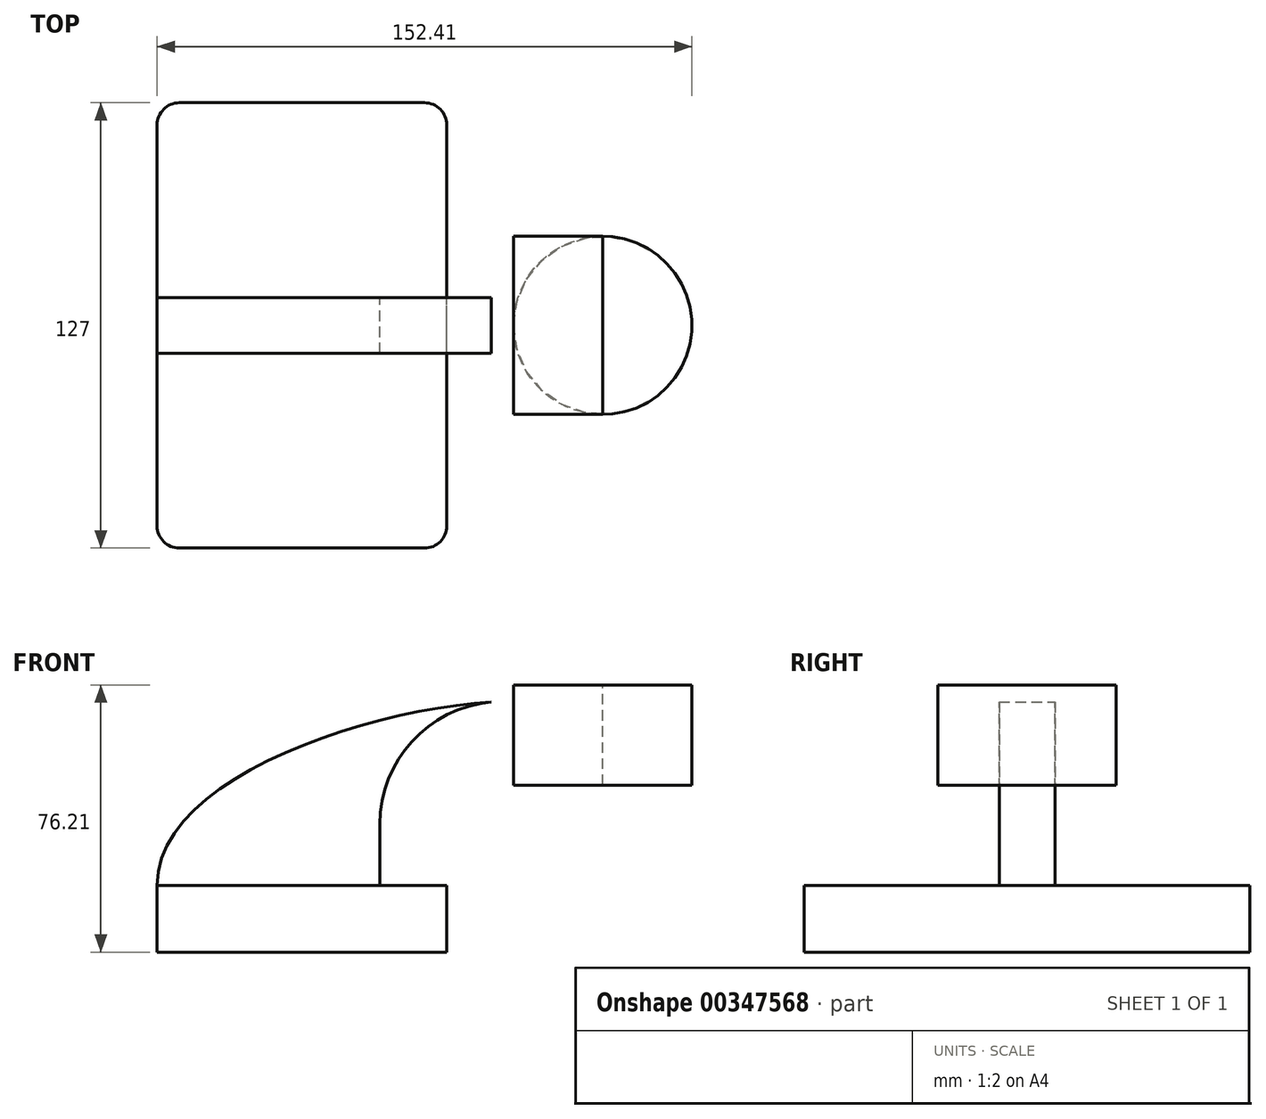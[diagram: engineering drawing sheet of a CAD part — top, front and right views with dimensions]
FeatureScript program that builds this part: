
annotation { "Feature Type Name" : "Feature", "Feature Type Description" : "" }
export const myFeature = defineFeature(function(context is Context, id is Id, definition is map)
    precondition{}
    {
        {
            var Q0;
            Q0=qCreatedBy(makeId("Front.planeOp"),FACE);
            var sketch = newSketch(context, id + "F0", { "sketchPlane" : qUnion([Q0])});
            skLineSegment(sketch, "E0.bottom", {"start": v(-41.28, 9.52) * mm, "end": v(41.27, 9.53) * mm});
            skLineSegment(sketch, "E0.top", {"start": v(-41.28, -9.53) * mm, "end": v(41.28, -9.53) * mm});
            skLineSegment(sketch, "E0.left", {"start": v(-41.28, 9.52) * mm, "end": v(-41.27, -9.53) * mm});
            skLineSegment(sketch, "E0.right", {"start": v(41.28, 9.53) * mm, "end": v(41.28, -9.52) * mm});
            skPoint(sketch, "E0.middle", {"position": v(0, 0) * mm});
            skLineSegment(sketch, "E1.bottom", {"start": v(60.32, 66.68) * mm, "end": v(111.12, 66.68) * mm});
            skLineSegment(sketch, "E1.top", {"start": v(60.32, 38.1) * mm, "end": v(111.12, 38.1) * mm});
            skLineSegment(sketch, "E1.left", {"start": v(60.32, 66.68) * mm, "end": v(60.32, 38.1) * mm});
            skLineSegment(sketch, "E1.right", {"start": v(111.12, 66.68) * mm, "end": v(111.12, 38.1) * mm});
            skPoint(sketch, "E1.middle", {"position": v(85.72, 52.39) * mm});
            skArc(sketch, "E2", {"start": v(41.27, 27) * mm, "mid": v(45.92, 38.23) * mm, "end": v(57.15, 42.88) * mm});
            skLineSegment(sketch, "E3", {"start": v(57.15, 42.88) * mm, "end": v(85.71, 42.88) * mm});
            skLineSegment(sketch, "E4", {"start": v(41.27, 27) * mm, "end": v(41.27, 9.53) * mm});
            skLineSegment(sketch, "E5.0", {"start": v(22.23, 27) * mm, "end": v(22.23, 9.53) * mm});
            skLineSegment(sketch, "E6.0", {"start": v(57.15, 61.93) * mm, "end": v(85.71, 61.93) * mm});
            skArc(sketch, "E6.1", {"start": v(22.22, 27) * mm, "mid": v(32.45, 51.7) * mm, "end": v(57.15, 61.93) * mm});
            skLineSegment(sketch, "E7", {"start": v(85.72, 38.1) * mm, "end": v(85.71, 66.68) * mm});
            skFitSpline(sketch, "E8", {"points": [v(-41.28, 9.52) * mm, v(57.15, 61.93) * mm], "startDerivative": vector(-0.23, 93.6) * mm, "endDerivative": vector(107.82, 3.43) * mm});
            skSolve(sketch);
        }
        {
            var Q0;
            Q0=makeQuery(id+"F0.imprint","IMPRINT",FACE,{"disambiguationData":[TD([[makeQuery(id+"F0.imprint","IMPRINT",EDGE,{"derivedFrom":sQuery(id+"F0.wireOp",EDGE,"E0.top")}),1.0]])]});
            extrude(context, id + "F1", {"entities" : qUnion([Q0]), "endBound" : BoundingType.SYMMETRIC, "depth" : 127 * mm});
        }
        {
            var Q0;
            {var subQ4=sQuery(id+"F0.wireOp",EDGE,"E7");Q0=makeQuery(id+"F0.imprint","IMPRINT",FACE,{"disambiguationData":[TD([[makeQuery(id+"F0.imprint","IMPRINT",EDGE,{"derivedFrom":subQ4}),1.0]])]});}
            var Q1;
            {var subQ1=sQuery(id+"F0.wireOp",EDGE,"E2");Q1=makeQuery(id+"F0.imprint","IMPRINT",FACE,{"disambiguationData":[TD([[makeQuery(id+"F0.imprint","IMPRINT",EDGE,{"derivedFrom":subQ1}),1.0]])]});}
            extrude(context, id + "F2", {"entities" : qUnion([Q0, Q1]), "operationType" : NewBodyOperationType.ADD, "endBound" : BoundingType.SYMMETRIC, "depth" : 50.8 * mm});
        }
        {
            var Q0;
            {var subQ3=sQuery(id+"F0.wireOp",EDGE,"E5.0");Q0=makeQuery(id+"F0.imprint","IMPRINT",FACE,{"disambiguationData":[TD([[makeQuery(id+"F0.imprint","IMPRINT",EDGE,{"derivedFrom":subQ3}),-1.0]])]});}
            extrude(context, id + "F3", {"entities" : qUnion([Q0]), "operationType" : NewBodyOperationType.ADD, "endBound" : BoundingType.SYMMETRIC, "depth" : 15.88 * mm});
        }
        {
            var Q0;
            {var subQ0=sQuery(id+"F0.wireOp",EDGE,"E1.right");Q0=makeQuery(id+"F0.imprint","IMPRINT",FACE,{"disambiguationData":[TD([[makeQuery(id+"F0.imprint","IMPRINT",EDGE,{"derivedFrom":subQ0}),-1.0]])]});}
            var Q1;
            Q1=sQuery(id+"F0.wireOp",EDGE,"E7");
            revolve(context, id + "F4", {"entities" : qUnion([Q0]), "axis" : qUnion([Q1]), "revolveType" : RevolveType.FULL});
        }
        {
            var Q0;
            Q0=makeQuery(id+"F1.opExtrude","CAP_EDGE",EDGE,{"disambiguationData":[OSD([sQuery(id+"F0.wireOp",EDGE,"E0.right")])],"isStart":false});
            var Q1;
            Q1=makeQuery(id+"F1.opExtrude","CAP_EDGE",EDGE,{"disambiguationData":[OSD([sQuery(id+"F0.wireOp",EDGE,"E0.left")])],"isStart":false});
            var Q2;
            Q2=makeQuery(id+"F1.opExtrude","CAP_EDGE",EDGE,{"disambiguationData":[OSD([sQuery(id+"F0.wireOp",EDGE,"E0.right")])],"isStart":true});
            var Q3;
            Q3=makeQuery(id+"F1.opExtrude","CAP_EDGE",EDGE,{"disambiguationData":[OSD([sQuery(id+"F0.wireOp",EDGE,"E0.left")])],"isStart":true});
            fillet(context, id + "F5", {"entities" : qUnion([Q0, Q1, Q2, Q3]), "radius" : 6.35 * mm, "tangentPropagation" : true, "allowEdgeOverflow" : false});
        }
    });
